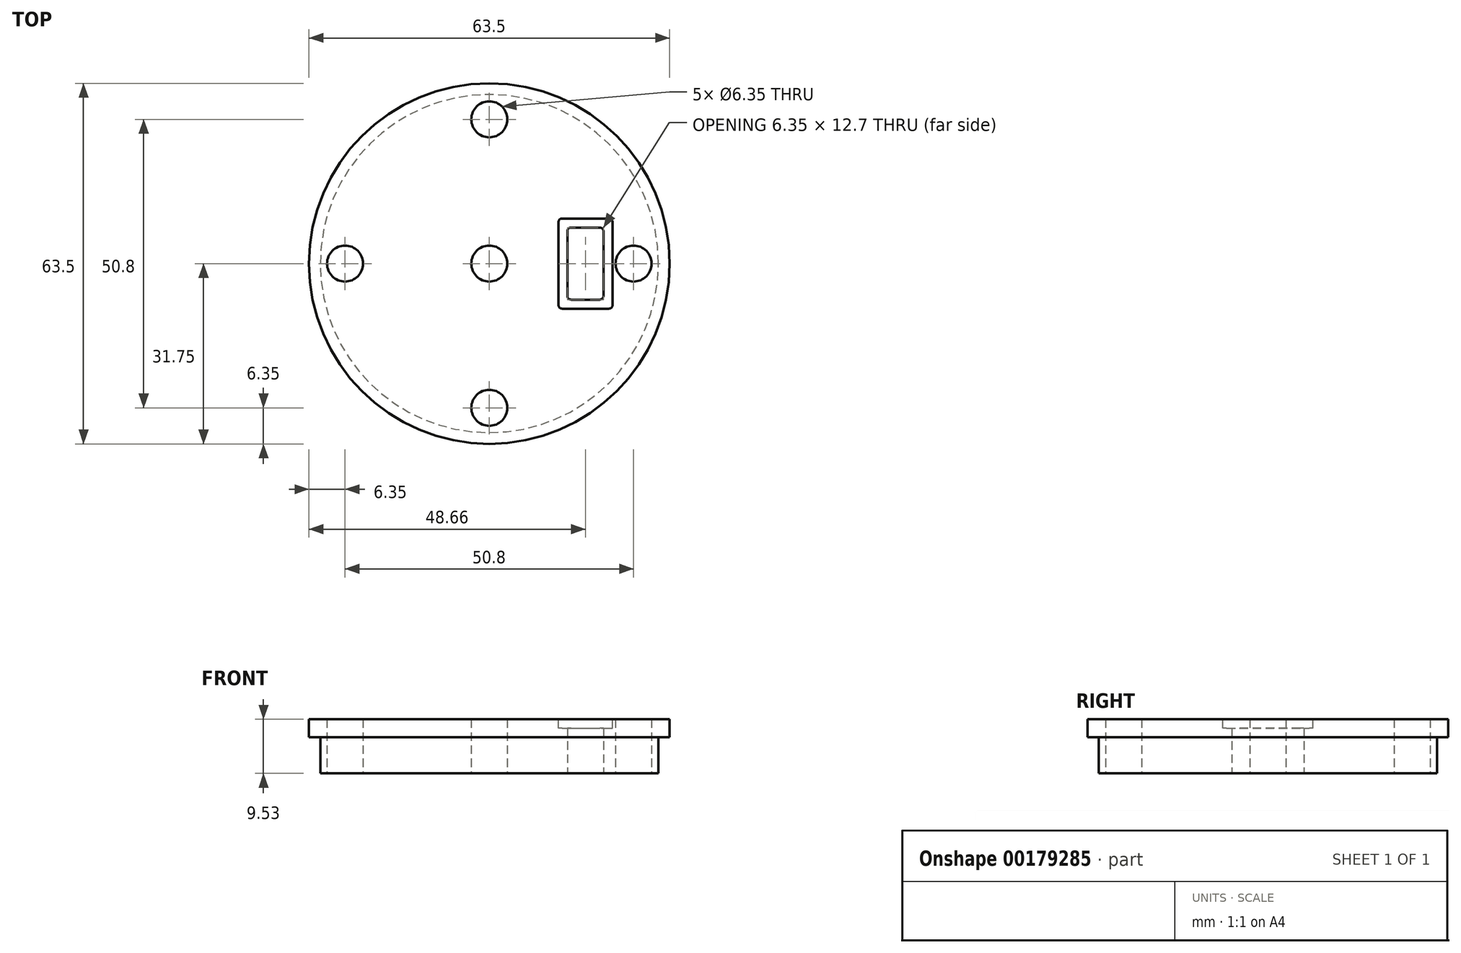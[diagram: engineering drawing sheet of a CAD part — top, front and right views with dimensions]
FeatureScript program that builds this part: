
annotation { "Feature Type Name" : "Feature", "Feature Type Description" : "" }
export const myFeature = defineFeature(function(context is Context, id is Id, definition is map)
    precondition{}
    {
        {
            var Q0;
            Q0=qCreatedBy(makeId("Top.planeOp"),FACE);
            var sketch = newSketch(context, id + "F0", { "sketchPlane" : qUnion([Q0])});
            skCircle(sketch, "E0", {"center": v(0, 0) * mm, "radius": 31.75 * mm});
            skCircle(sketch, "E1", {"center": v(0, 25.4) * mm, "radius": 3.18 * mm});
            skCircle(sketch, "E2", {"center": v(0, -25.4) * mm, "radius": 3.18 * mm});
            skCircle(sketch, "E3", {"center": v(25.4, 0) * mm, "radius": 3.18 * mm});
            skCircle(sketch, "E4", {"center": v(-25.4, 0) * mm, "radius": 3.18 * mm});
            skSolve(sketch);
        }
        {
            var Q0;
            Q0=makeQuery(id+"F0.imprint","IMPRINT",FACE,{"disambiguationData":[TD([[makeQuery(id+"F0.imprint","IMPRINT",EDGE,{"derivedFrom":sQuery(id+"F0.wireOp",EDGE,"E0")}),1.0]])]});
            extrude(context, id + "F1", {"entities" : qUnion([Q0]), "depth" : 9.52 * mm});
        }
        {
            var Q0;
            Q0=makeQuery(id+"F1.opExtrude","CAP_FACE",FACE,{"disambiguationData":[OSD([sQuery(id+"F0.wireOp",EDGE,"E0"),sQuery(id+"F0.wireOp",EDGE,"E1"),sQuery(id+"F0.wireOp",EDGE,"E2"),sQuery(id+"F0.wireOp",EDGE,"E3"),sQuery(id+"F0.wireOp",EDGE,"E4")])],"isStart":true});
            var sketch = newSketch(context, id + "F2", { "sketchPlane" : qUnion([Q0])});
            skCircle(sketch, "E5", {"center": v(0, 0) * mm, "radius": 29.77 * mm});
            skSolve(sketch);
        }
        {
            var Q0;
            Q0=makeQuery(id+"F2.imprint","IMPRINT",FACE,{"disambiguationData":[TD([[makeQuery(id+"F2.imprint","IMPRINT",EDGE,{"derivedFrom":sQuery(id+"F2.wireOp",EDGE,"E5")}),-1.0]])]});
            extrude(context, id + "F3", {"entities" : qUnion([Q0]), "operationType" : NewBodyOperationType.REMOVE, "oppositeDirection" : true, "depth" : 6.35 * mm});
        }
        {
            var Q0;
            Q0=makeQuery(id+"F1.opExtrude","CAP_FACE",FACE,{"disambiguationData":[OSD([sQuery(id+"F0.wireOp",EDGE,"E0"),sQuery(id+"F0.wireOp",EDGE,"E1"),sQuery(id+"F0.wireOp",EDGE,"E2"),sQuery(id+"F0.wireOp",EDGE,"E3"),sQuery(id+"F0.wireOp",EDGE,"E4")])],"isStart":true});
            var sketch = newSketch(context, id + "F4", { "sketchPlane" : qUnion([Q0])});
            skCircle(sketch, "E6", {"center": v(0, 0) * mm, "radius": 3.18 * mm});
            skSolve(sketch);
        }
        {
            var Q0;
            Q0 = qSketchRegion(id + "F4", true);
            extrude(context, id + "F5", {"entities" : qUnion([Q0]), "operationType" : NewBodyOperationType.REMOVE, "endBound" : BoundingType.THROUGH_ALL, "oppositeDirection" : true, "depth" : 25.4 * mm});
        }
        {
            var Q0;
            Q0=makeQuery(id+"F1.opExtrude","CAP_FACE",FACE,{"disambiguationData":[OSD([sQuery(id+"F0.wireOp",EDGE,"E0"),sQuery(id+"F0.wireOp",EDGE,"E1"),sQuery(id+"F0.wireOp",EDGE,"E2"),sQuery(id+"F0.wireOp",EDGE,"E3"),sQuery(id+"F0.wireOp",EDGE,"E4")])],"isStart":true});
            var sketch = newSketch(context, id + "F6", { "sketchPlane" : qUnion([Q0])});
            skLineSegment(sketch, "E7.bottom", {"start": v(13.73, -6.35) * mm, "end": v(20.08, -6.35) * mm});
            skLineSegment(sketch, "E7.top", {"start": v(13.73, 6.35) * mm, "end": v(20.08, 6.35) * mm});
            skLineSegment(sketch, "E7.left", {"start": v(13.73, -6.35) * mm, "end": v(13.73, 6.35) * mm});
            skLineSegment(sketch, "E7.right", {"start": v(20.08, -6.35) * mm, "end": v(20.08, 6.35) * mm});
            skPoint(sketch, "E7.middle", {"position": v(16.9, 0) * mm});
            skSolve(sketch);
        }
        {
            var Q0;
            Q0 = qSketchRegion(id + "F6", true);
            extrude(context, id + "F7", {"entities" : qUnion([Q0]), "operationType" : NewBodyOperationType.REMOVE, "oppositeDirection" : true, "depth" : 25.4 * mm});
        }
        {
            var Q0;
            Q0=makeQuery(id+"F1.opExtrude","CAP_FACE",FACE,{"disambiguationData":[OSD([sQuery(id+"F0.wireOp",EDGE,"E0"),sQuery(id+"F0.wireOp",EDGE,"E1"),sQuery(id+"F0.wireOp",EDGE,"E2"),sQuery(id+"F0.wireOp",EDGE,"E3"),sQuery(id+"F0.wireOp",EDGE,"E4")])],"isStart":false});
            var sketch = newSketch(context, id + "F8", { "sketchPlane" : qUnion([Q0])});
            skLineSegment(sketch, "E8.bottom", {"start": v(12.18, -7.94) * mm, "end": v(21.7, -7.94) * mm});
            skLineSegment(sketch, "E8.top", {"start": v(12.18, 7.94) * mm, "end": v(21.7, 7.94) * mm});
            skLineSegment(sketch, "E8.left", {"start": v(12.18, -7.94) * mm, "end": v(12.18, 7.94) * mm});
            skLineSegment(sketch, "E8.right", {"start": v(21.7, -7.94) * mm, "end": v(21.7, 7.94) * mm});
            skPoint(sketch, "E8.middle", {"position": v(16.94, 0) * mm});
            skPoint(sketch, "E8.middle.positionSnap0", {"position": v(13.73, 0) * mm});
            skPoint(sketch, "E8.centerSnap0", {"position": v(13.73, 0) * mm});
            skSolve(sketch);
        }
        {
            var Q0;
            Q0 = qSketchRegion(id + "F8", true);
            extrude(context, id + "F9", {"entities" : qUnion([Q0]), "operationType" : NewBodyOperationType.REMOVE, "oppositeDirection" : true, "depth" : 1.57 * mm});
        }
        {
            var Q0;
            Q0=makeQuery(id+"F7.boolean.opBoolean","COPY",EDGE,{"derivedFrom":makeQuery(id+"F7.opExtrude","SWEPT_EDGE",EDGE,{"disambiguationData":[OSD([sQuery(id+"F6.wireOp",EDGE,"E7.top"),sQuery(id+"F6.wireOp",EDGE,"E7.left")])]})});
            var Q1;
            Q1=makeQuery(id+"F7.boolean.opBoolean","COPY",EDGE,{"derivedFrom":makeQuery(id+"F7.opExtrude","SWEPT_EDGE",EDGE,{"disambiguationData":[OSD([sQuery(id+"F6.wireOp",EDGE,"E7.bottom"),sQuery(id+"F6.wireOp",EDGE,"E7.left")])]})});
            var Q2;
            Q2=makeQuery(id+"F7.boolean.opBoolean","COPY",EDGE,{"derivedFrom":makeQuery(id+"F7.opExtrude","SWEPT_EDGE",EDGE,{"disambiguationData":[OSD([sQuery(id+"F6.wireOp",EDGE,"E7.top"),sQuery(id+"F6.wireOp",EDGE,"E7.right")])]})});
            var Q3;
            Q3=makeQuery(id+"F7.boolean.opBoolean","COPY",EDGE,{"derivedFrom":makeQuery(id+"F7.opExtrude","SWEPT_EDGE",EDGE,{"disambiguationData":[OSD([sQuery(id+"F6.wireOp",EDGE,"E7.bottom"),sQuery(id+"F6.wireOp",EDGE,"E7.right")])]})});
            var Q4;
            Q4=makeQuery(id+"F9.boolean.opBoolean","COPY",EDGE,{"derivedFrom":makeQuery(id+"F9.opExtrude","SWEPT_EDGE",EDGE,{"disambiguationData":[OSD([sQuery(id+"F8.wireOp",EDGE,"E8.top"),sQuery(id+"F8.wireOp",EDGE,"E8.right")])]})});
            var Q5;
            Q5=makeQuery(id+"F9.boolean.opBoolean","COPY",EDGE,{"derivedFrom":makeQuery(id+"F9.opExtrude","SWEPT_EDGE",EDGE,{"disambiguationData":[OSD([sQuery(id+"F8.wireOp",EDGE,"E8.bottom"),sQuery(id+"F8.wireOp",EDGE,"E8.right")])]})});
            var Q6;
            Q6=makeQuery(id+"F9.boolean.opBoolean","COPY",EDGE,{"derivedFrom":makeQuery(id+"F9.opExtrude","SWEPT_EDGE",EDGE,{"disambiguationData":[OSD([sQuery(id+"F8.wireOp",EDGE,"E8.bottom"),sQuery(id+"F8.wireOp",EDGE,"E8.left")])]})});
            var Q7;
            Q7=makeQuery(id+"F9.boolean.opBoolean","COPY",EDGE,{"derivedFrom":makeQuery(id+"F9.opExtrude","SWEPT_EDGE",EDGE,{"disambiguationData":[OSD([sQuery(id+"F8.wireOp",EDGE,"E8.top"),sQuery(id+"F8.wireOp",EDGE,"E8.left")])]})});
            fillet(context, id + "F10", {"entities" : qUnion([Q0, Q1, Q2, Q3, Q4, Q5, Q6, Q7]), "radius" : 0.64 * mm, "tangentPropagation" : true, "allowEdgeOverflow" : false});
        }
    });
